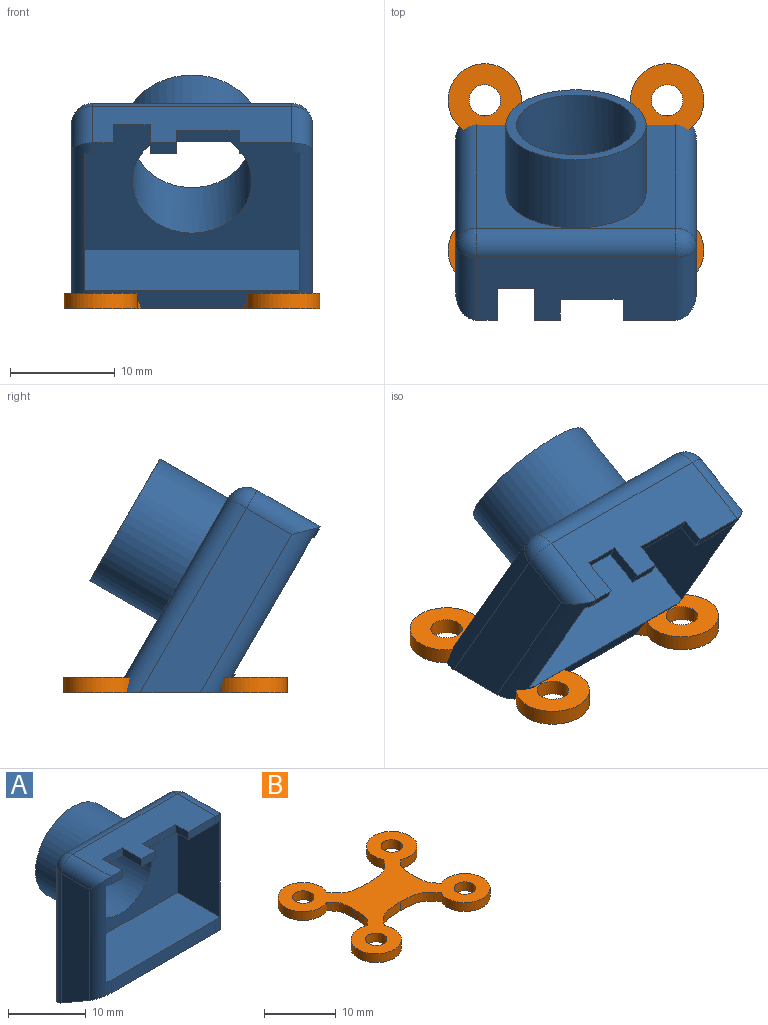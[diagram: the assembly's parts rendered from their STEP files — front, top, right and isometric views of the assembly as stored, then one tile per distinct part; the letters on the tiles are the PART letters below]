
ASSEMBLY  parts=2 mates=1
PART A: 32 faces, bbox 23x16.5x23.5 mm
  f0: plane 19x2mm, normal (0,-1,0), area 38.1mm2, adj f9,f22,f23,f29
  f1: plane 2x1.2mm, normal (0,-1,0), area 2.4mm2, adj f5,f6,f16,f23
  f2: plane 5x1.2mm, normal (0,-1,0), area 6mm2, adj f5,f6,f19,f29
  f3: plane 20.35x5mm, normal (1,0,0), area 94.5mm2, adj f22,f28,f29,f31
  f4: plane 2.5x1.2mm, normal (0,-1,0), area 3mm2, adj f5,f6,f17,f21
  f5: plane 19x7mm, normal (0,0,1), area 106.9mm2, adj f1,f2,f4,f16,f17,f18,f19,f20
  f6: plane 20.6x7.8mm, normal (0,0,-1), area 134.5mm2, adj f1,f2,f4,f10,f11,f12,f16,f17
  f7: plane 20.35x5mm, normal (-1,0,0), area 94.5mm2, adj f22,f23,f24,f25
  f8: plane 21.5x19mm, normal (0,1,0), area 267.5mm2, adj f14,f22,f25,f27,f28
  f9: plane 20.6x7.8mm, normal (0,0,1), area 160.6mm2, adj f0,f10,f11,f12,f23,f29
  f10: plane 15.1x7.63mm, normal (-1,0,0), area 115.3mm2, adj f6,f9,f12,f29
  f11: plane 15.1x7.63mm, normal (1,0,0), area 115.3mm2, adj f6,f9,f12,f23
  f12: plane 20.6x15.1mm, normal (0,-1,0), area 209mm2, adj f6,f9,f10,f11,f13
  f13: cylinder r=5.7mm len=11.4mm, axis (0,1,0), area 311.6mm2, adj f12,f15
  f14: cylinder r=6.7mm len=13.4mm, axis (0,-1,0), area 315.7mm2, adj f8,f15
  f15: plane 13.4x13.4mm, normal (0,1,0), area 39mm2, adj f13,f14
  f16: plane 3.5x1.2mm, normal (1,0,0), area 4.2mm2, adj f1,f5,f6,f18
  f17: plane 3.5x1.2mm, normal (-1,0,0), area 4.2mm2, adj f4,f5,f6,f18
  f18: plane 3.5x1.2mm, normal (0,-1,0), area 4.2mm2, adj f5,f6,f16,f17
  f19: plane 2.3x1.2mm, normal (-1,0,0), area 2.8mm2, adj f2,f5,f6,f20
  f20: plane 6x1.2mm, normal (0,-1,0), area 7.2mm2, adj f5,f6,f19,f21
  f21: plane 2.3x1.2mm, normal (1,0,0), area 2.8mm2, adj f4,f5,f6,f20
  f22: plane 23x9mm, normal (0,-0.5,-0.87), area 235.1mm2, adj f0,f3,f7,f8,f23,f25,f28,f29
  f23: cylinder r=2mm len=19.46mm, axis (0,0,1), area 44.1mm2, adj f0,f1,f6,f7,f9,f11,f22,f24
  f24: cylinder r=2mm len=7mm, axis (0,-1,0), area 19.7mm2, adj f5,f7,f23,f26
  f25: cylinder r=2mm len=21.5mm, axis (0,0,-1), area 66.2mm2, adj f7,f8,f22,f26
  f26: sphere r=2mm, area 6.3mm2, adj f24,f25,f27
  f27: cylinder r=2mm len=19mm, axis (-1,0,0), area 59.7mm2, adj f5,f8,f26,f30
  f28: cylinder r=2mm len=21.5mm, axis (0,0,1), area 66.2mm2, adj f3,f8,f22,f30
  f29: cylinder r=2mm len=19.46mm, axis (0,0,-1), area 44.1mm2, adj f0,f2,f3,f6,f9,f10,f22,f31
  f30: sphere r=2mm, area 6.3mm2, adj f27,f28,f31
  f31: cylinder r=2mm len=7mm, axis (0,1,0), area 19.7mm2, adj f3,f5,f29,f30
PART B: 18 faces, bbox 24.4x21.4x1.5 mm
  f0: extruded ~5.56x2.48mm, area 9.7mm2, adj f1,f12,f16,f17
  f1: cylinder r=3.5mm len=7mm, axis (0,0,-1), area 29.4mm2, adj f0,f2,f16,f17
  f2: extruded ~4x1.5mm, area 6.7mm2, adj f1,f3,f16,f17
  f3: extruded ~4x1.5mm, area 6.7mm2, adj f2,f4,f16,f17
  f4: cylinder r=3.5mm len=7mm, axis (0,0,-1), area 29.4mm2, adj f3,f5,f16,f17
  f5: extruded ~5.56x2.48mm, area 9.7mm2, adj f4,f6,f16,f17
  f6: extruded ~5.56x2.48mm, area 9.7mm2, adj f5,f7,f16,f17
  f7: cylinder r=3.5mm len=7mm, axis (0,0,-1), area 29.4mm2, adj f6,f8,f16,f17
  f8: extruded ~4x1.5mm, area 6.7mm2, adj f7,f9,f16,f17
  f9: extruded ~4x1.5mm, area 6.7mm2, adj f8,f10,f16,f17
  f10: cylinder r=3.5mm len=7mm, axis (0,0,-1), area 29.4mm2, adj f9,f12,f16,f17
  f11: cylinder r=1.5mm len=3mm, axis (0,0,-1), area 14.1mm2, adj f16,f17
  f12: extruded ~5.56x2.48mm, area 9.7mm2, adj f0,f10,f16,f17
  f13: cylinder r=1.5mm len=3mm, axis (0,0,-1), area 14.1mm2, adj f16,f17
  f14: cylinder r=1.5mm len=3mm, axis (0,0,-1), area 14.1mm2, adj f16,f17
  f15: cylinder r=1.5mm len=3mm, axis (0,0,-1), area 14.1mm2, adj f16,f17
  f16: plane 24.42x21.35mm, normal (0,0,1), area 222.7mm2, adj f0,f1,f2,f3,f4,f5,f6,f7
  f17: plane 24.42x21.35mm, normal (0,0,-1), area 222.7mm2, adj f0,f1,f2,f3,f4,f5,f6,f7
PLACE A rot(axis=(1,0,0),30deg) t=(0,-39.48,12.77)mm
PLACE B t=(0,-37.8,0)mm
MATE fastened A.f22 <-> B.f17  axis (0,0,-1) through (0,-37.3,0)mm
